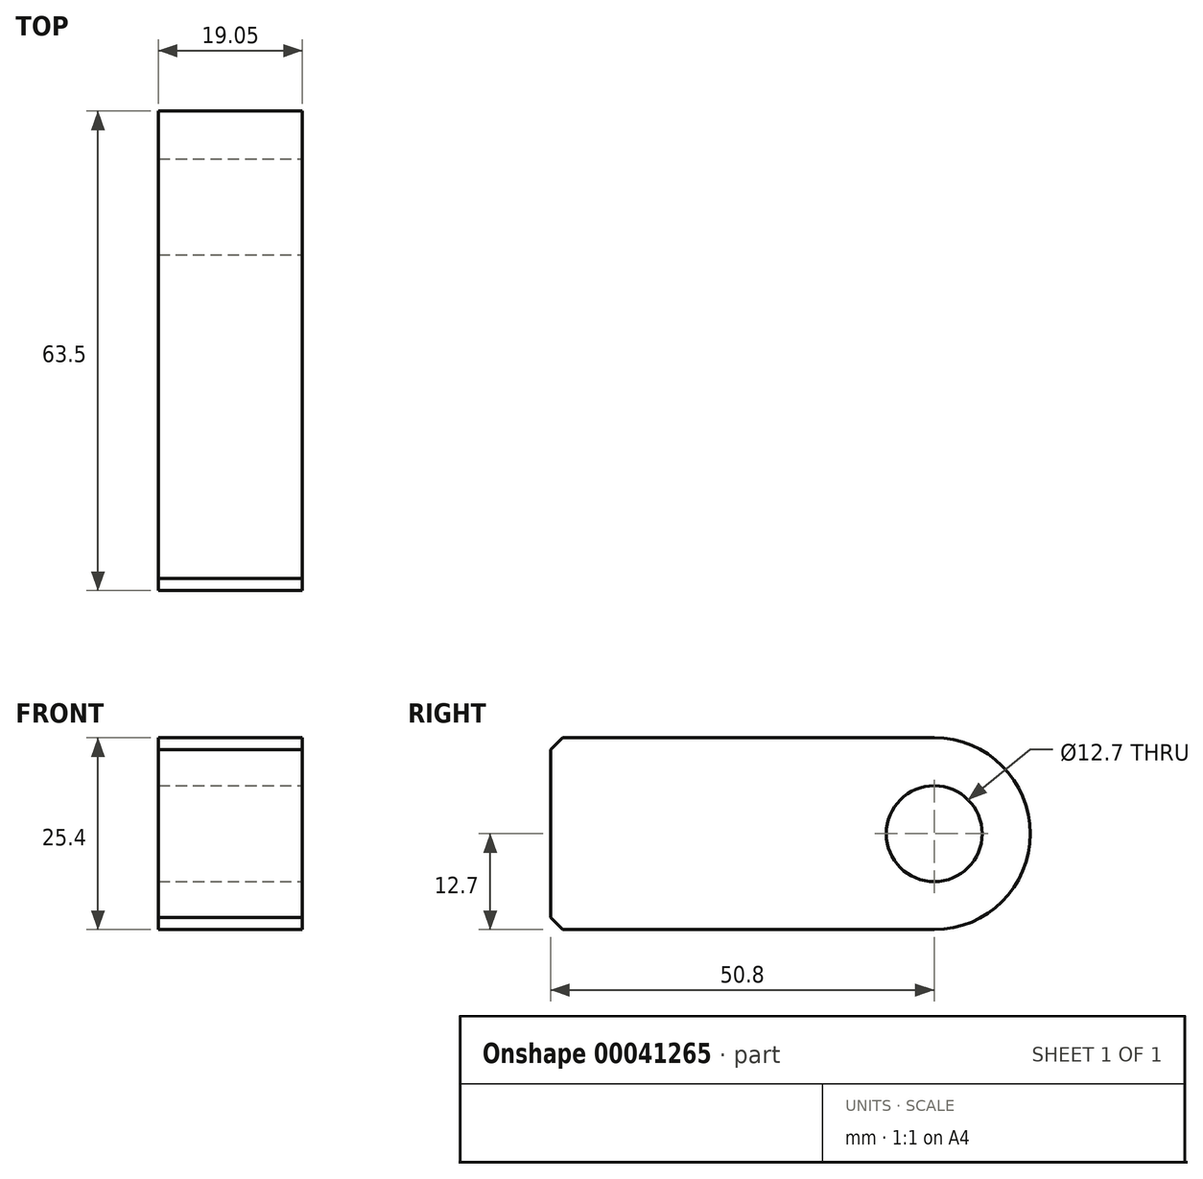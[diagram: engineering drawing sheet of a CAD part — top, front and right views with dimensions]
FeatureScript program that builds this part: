
annotation { "Feature Type Name" : "Feature", "Feature Type Description" : "" }
export const myFeature = defineFeature(function(context is Context, id is Id, definition is map)
    precondition{}
    {
        {
            var Q0;
            Q0=qCreatedBy(makeId("Right.planeOp"),FACE);
            var sketch = newSketch(context, id + "F0", { "sketchPlane" : qUnion([Q0])});
            skLineSegment(sketch, "E0.rect.bottom", {"start": v(31.75, 12.7) * mm, "end": v(-31.75, 12.7) * mm});
            skLineSegment(sketch, "E0.rect.top", {"start": v(31.75, -12.7) * mm, "end": v(-31.75, -12.7) * mm});
            skLineSegment(sketch, "E0.rect.left", {"start": v(31.75, 12.7) * mm, "end": v(31.75, -12.7) * mm});
            skLineSegment(sketch, "E0.rect.right", {"start": v(-31.75, 12.7) * mm, "end": v(-31.75, -12.7) * mm});
            skPoint(sketch, "E0.rect.middle", {"position": v(0, 0) * mm});
            skSolve(sketch);
        }
        {
            var Q0;
            Q0=makeQuery(id+"F0.imprint","IMPRINT",FACE,{"disambiguationData":[TD([[makeQuery(id+"F0.imprint","IMPRINT",EDGE,{"derivedFrom":sQuery(id+"F0.wireOp",EDGE,"E0.rect.bottom")}),1.0]])]});
            extrude(context, id + "F1", {"entities" : qUnion([Q0]), "depth" : 19.05 * mm});
        }
        {
            var Q0;
            Q0=makeQuery(id+"F1.opExtrude","CAP_FACE",FACE,{"disambiguationData":[OSD([sQuery(id+"F0.wireOp",EDGE,"E0.rect.bottom"),sQuery(id+"F0.wireOp",EDGE,"E0.rect.top"),sQuery(id+"F0.wireOp",EDGE,"E0.rect.left"),sQuery(id+"F0.wireOp",EDGE,"E0.rect.right")])],"isStart":false});
            var sketch = newSketch(context, id + "F2", { "sketchPlane" : qUnion([Q0])});
            skCircle(sketch, "E1", {"center": v(19.05, 0) * mm, "radius": 6.35 * mm});
            skSolve(sketch);
        }
        {
            var Q0;
            Q0=makeQuery(id+"F2.imprint","IMPRINT",FACE,{"disambiguationData":[TD([[makeQuery(id+"F2.imprint","IMPRINT",EDGE,{"derivedFrom":sQuery(id+"F2.wireOp",EDGE,"E1")}),1.0]])]});
            extrude(context, id + "F3", {"entities" : qUnion([Q0]), "operationType" : NewBodyOperationType.REMOVE, "oppositeDirection" : true, "depth" : 25.4 * mm});
        }
        {
            var Q0;
            Q0=makeQuery(id+"F1.opExtrude","SWEPT_EDGE",EDGE,{"disambiguationData":[OSD([sQuery(id+"F0.wireOp",EDGE,"E0.rect.bottom"),sQuery(id+"F0.wireOp",EDGE,"E0.rect.left")])]});
            var Q1;
            Q1=makeQuery(id+"F1.opExtrude","SWEPT_EDGE",EDGE,{"disambiguationData":[OSD([sQuery(id+"F0.wireOp",EDGE,"E0.rect.top"),sQuery(id+"F0.wireOp",EDGE,"E0.rect.left")])]});
            fillet(context, id + "F4", {"entities" : qUnion([Q0, Q1]), "radius" : 12.7 * mm, "tangentPropagation" : true, "allowEdgeOverflow" : false});
        }
        {
            var Q0;
            Q0=makeQuery(id+"F1.opExtrude","SWEPT_EDGE",EDGE,{"disambiguationData":[OSD([sQuery(id+"F0.wireOp",EDGE,"E0.rect.bottom"),sQuery(id+"F0.wireOp",EDGE,"E0.rect.right")])]});
            var Q1;
            Q1=makeQuery(id+"F1.opExtrude","SWEPT_EDGE",EDGE,{"disambiguationData":[OSD([sQuery(id+"F0.wireOp",EDGE,"E0.rect.top"),sQuery(id+"F0.wireOp",EDGE,"E0.rect.right")])]});
            chamfer(context, id + "F5", {"entities" : qUnion([Q0, Q1]), "width" : 1.59 * mm, "tangentPropagation" : true});
        }
    });
